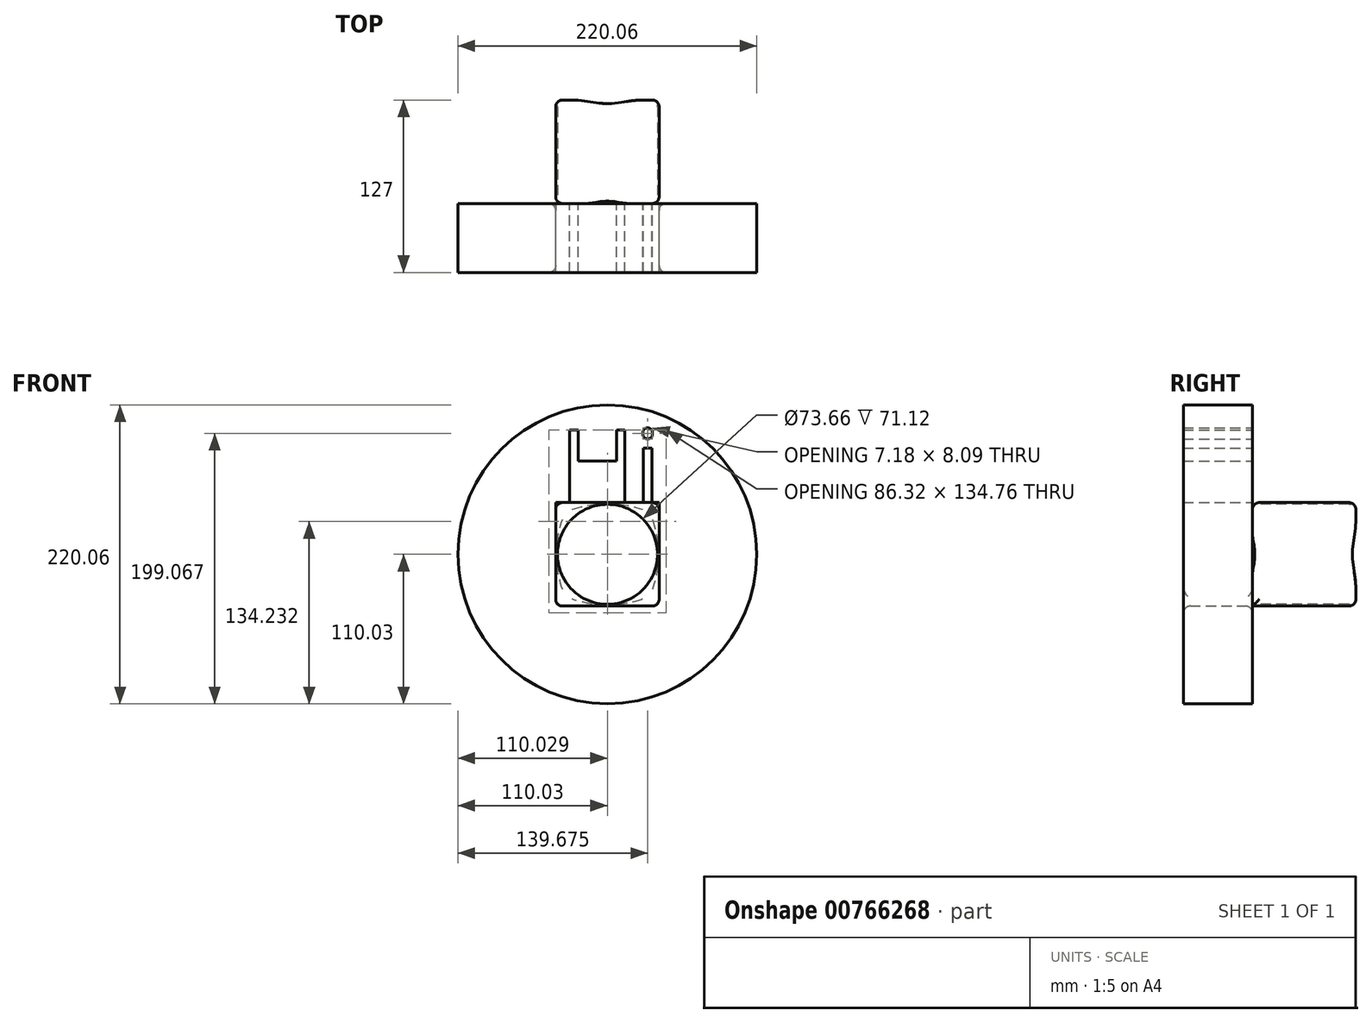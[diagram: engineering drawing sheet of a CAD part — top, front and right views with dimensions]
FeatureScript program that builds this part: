
annotation { "Feature Type Name" : "Feature", "Feature Type Description" : "" }
export const myFeature = defineFeature(function(context is Context, id is Id, definition is map)
    precondition{}
    {
        {
            var Q0;
            Q0=qCreatedBy(makeId("Front.planeOp"),FACE);
            var sketch = newSketch(context, id + "F0", { "sketchPlane" : qUnion([Q0])});
            skLineSegment(sketch, "E0.bottom", {"start": v(-92.56, 76.2) * mm, "end": v(-16.36, 76.2) * mm});
            skLineSegment(sketch, "E0.top", {"start": v(-92.56, 0) * mm, "end": v(-16.36, 0) * mm});
            skLineSegment(sketch, "E0.left", {"start": v(-92.56, 76.2) * mm, "end": v(-92.56, 0) * mm});
            skLineSegment(sketch, "E0.right", {"start": v(-16.36, 76.2) * mm, "end": v(-16.36, 0) * mm});
            skSolve(sketch);
        }
        {
            var Q0;
            Q0 = qSketchRegion(id + "F0", true);
            extrude(context, id + "F1", {"entities" : qUnion([Q0]), "depth" : 76.2 * mm, "offsetDistance" : 25.4 * mm});
        }
        {
            var Q0;
            Q0=makeQuery(id+"F1.opExtrude","CAP_FACE",FACE,{"disambiguationData":[OSD([sQuery(id+"F0.wireOp",EDGE,"E0.bottom"),sQuery(id+"F0.wireOp",EDGE,"E0.top"),sQuery(id+"F0.wireOp",EDGE,"E0.left"),sQuery(id+"F0.wireOp",EDGE,"E0.right")])],"isStart":false});
            var sketch = newSketch(context, id + "F2", { "sketchPlane" : qUnion([Q0])});
            skPoint(sketch, "E1", {"position": v(-54.46, 38.1) * mm});
            skCircle(sketch, "E2", {"center": v(-54.46, 38.1) * mm, "radius": 38 * mm});
            skCircle(sketch, "E3", {"center": v(-54.46, 38.1) * mm, "radius": 110.03 * mm});
            skText(sketch, "E4", { "text": "Hi", "fontName": "OpenSans-Regular.ttf"});
            const initialGuessF2  = {"E4": [-0.0896, 0.0762, 1, 0, 0.05394]};
            skSetInitialGuess(sketch, initialGuessF2);
            skSolve(sketch);
        }
        {
            var Q0;
            Q0=makeQuery(id+"F2.imprint","IMPRINT",FACE,{"disambiguationData":[TD([[makeQuery(id+"F2.imprint","IMPRINT",EDGE,{"derivedFrom":sQuery(id+"F2.wireOp",EDGE,"E3")}),1.0]])]});
            extrude(context, id + "F3", {"entities" : qUnion([Q0]), "depth" : 50.8 * mm, "offsetDistance" : 25.4 * mm});
        }
        {
            var Q0;
            Q0=makeQuery(id+"F1.opExtrude","CAP_FACE",FACE,{"disambiguationData":[OSD([sQuery(id+"F0.wireOp",EDGE,"E0.bottom"),sQuery(id+"F0.wireOp",EDGE,"E0.top"),sQuery(id+"F0.wireOp",EDGE,"E0.left"),sQuery(id+"F0.wireOp",EDGE,"E0.right")])],"isStart":false});
            var sketch = newSketch(context, id + "F4", { "sketchPlane" : qUnion([Q0])});
            skPoint(sketch, "E5", {"position": v(-54.46, 38.1) * mm});
            skSolve(sketch);
        }
        {
            var Q0;
            Q0=sQuery(id+"F4.wireOp",VERTEX,"E5");
            var Q1;
            Q1=makeQuery(id+"F1.opExtrude","SWEPT_BODY",BODY,{"disambiguationData":[OSD([sQuery(id+"F0.wireOp",EDGE,"E0.bottom"),sQuery(id+"F0.wireOp",EDGE,"E0.top"),sQuery(id+"F0.wireOp",EDGE,"E0.left"),sQuery(id+"F0.wireOp",EDGE,"E0.right")])]});
            hole(context, id + "F5", {"style" : HoleStyle.SIMPLE, "endStyle" : HoleEndStyle.THROUGH, "holeDiameter" : 73.66 * mm, "majorDiameter" : 6.35 * mm, "isTappedThrough" : true, "tappedDepth" : 12.7 * mm, "tapClearance" : 3, "locations" : qUnion([Q0]), "scope" : qUnion([Q1])});
        }
        {
            var Q0;
            Q0=makeQuery(id+"F1.opExtrude","CAP_EDGE",EDGE,{"disambiguationData":[OSD([sQuery(id+"F0.wireOp",EDGE,"E0.bottom")])],"isStart":true});
            var Q1;
            Q1=makeQuery(id+"F1.opExtrude","SWEPT_FACE",FACE,{"disambiguationData":[OSD([sQuery(id+"F0.wireOp",EDGE,"E0.bottom")])]});
            var Q2;
            Q2=makeQuery(id+"F5.hole-0.boolean.opBoolean","COPY",FACE,{"derivedFrom":makeQuery(id+"F5.hole-0.opRevolve","SWEPT_FACE",FACE,{"disambiguationData":[OSD([sQuery(id+"F5.hole-0.sketch.wireOp",EDGE,"core_line_2")])]})});
            var Q3;
            Q3=makeQuery(id+"F1.opExtrude","CAP_EDGE",EDGE,{"disambiguationData":[OSD([sQuery(id+"F0.wireOp",EDGE,"E0.right")])],"isStart":true});
            var Q4;
            Q4=makeQuery(id+"F1.opExtrude","CAP_FACE",FACE,{"disambiguationData":[OSD([sQuery(id+"F0.wireOp",EDGE,"E0.bottom"),sQuery(id+"F0.wireOp",EDGE,"E0.top"),sQuery(id+"F0.wireOp",EDGE,"E0.left"),sQuery(id+"F0.wireOp",EDGE,"E0.right")])],"isStart":true});
            var Q5;
            Q5=makeQuery(id+"F3.opExtrude","SWEPT_FACE",FACE,{"disambiguationData":[OSD([sQuery(id+"F2.wireOp",EDGE,"E3")])]});
            var Q6;
            Q6=makeQuery(id+"F3.opExtrude","SWEPT_FACE",FACE,{"disambiguationData":[OSD([sQuery(id+"F0.wireOp",EDGE,"E0.bottom")])]});
            var Q7;
            Q7=makeQuery(id+"F1.opExtrude","SWEPT_FACE",FACE,{"disambiguationData":[OSD([sQuery(id+"F0.wireOp",EDGE,"E0.left")])]});
            var Q8;
            Q8=makeQuery(id+"F1.opExtrude","SWEPT_FACE",FACE,{"disambiguationData":[OSD([sQuery(id+"F0.wireOp",EDGE,"E0.right")])]});
            fillet(context, id + "F6", {"entities" : qUnion([Q0, Q1, Q2, Q3, Q4, Q5, Q6, Q7, Q8]), "radius" : 5.08 * mm, "tangentPropagation" : true, "allowEdgeOverflow" : false});
        }
        {
            var Q0;
            Q0=makeQuery(id+"F3.opExtrude","SWEPT_FACE",FACE,{"disambiguationData":[OSD([sQuery(id+"F0.wireOp",EDGE,"E0.top")])]});
            fillet(context, id + "F7", {"entities" : qUnion([Q0]), "radius" : 5.08 * mm, "tangentPropagation" : true, "allowEdgeOverflow" : false});
        }
    });
